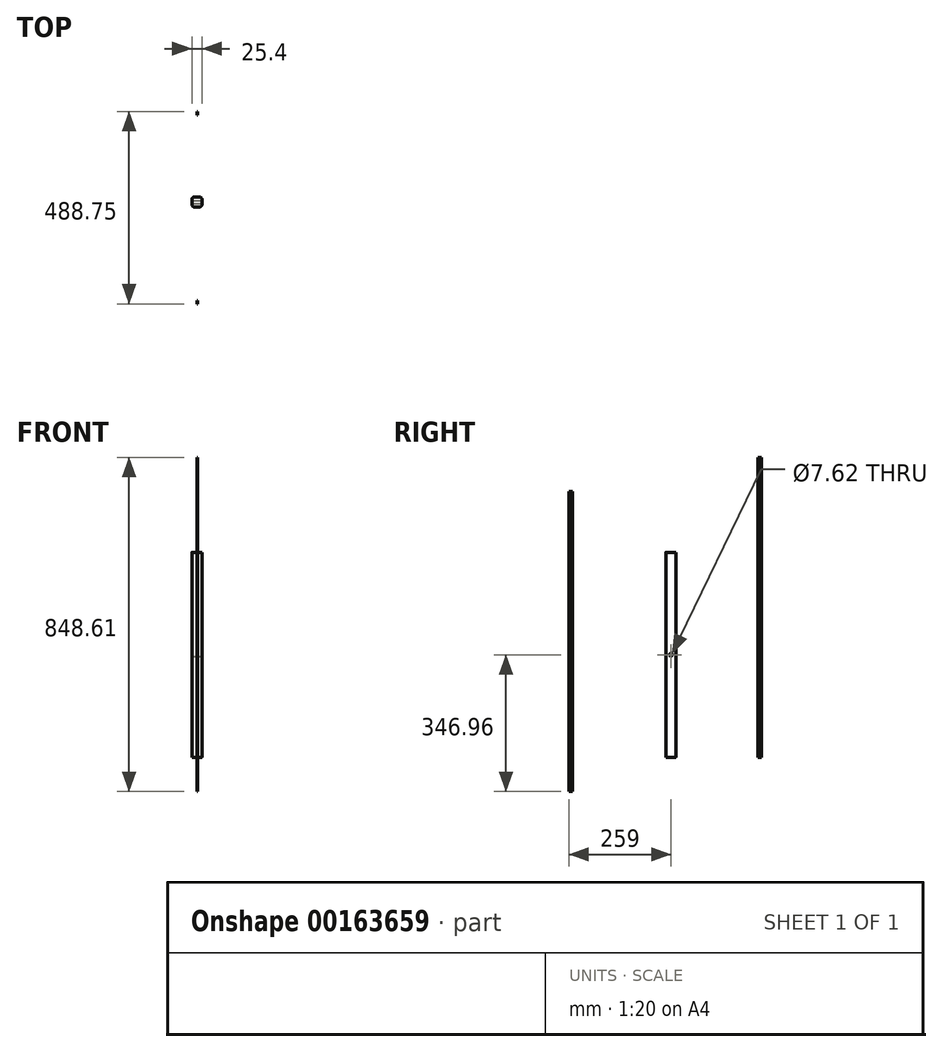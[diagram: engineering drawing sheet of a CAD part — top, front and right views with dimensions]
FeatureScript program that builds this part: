
annotation { "Feature Type Name" : "Feature", "Feature Type Description" : "" }
export const myFeature = defineFeature(function(context is Context, id is Id, definition is map)
    precondition{}
    {
        {
            var Q0;
            Q0=qCreatedBy(makeId("Top.planeOp"),FACE);
            var sketch = newSketch(context, id + "F0", { "sketchPlane" : qUnion([Q0])});
            skLineSegment(sketch, "E0.bottom", {"start": v(6.35, 12.7) * mm, "end": v(-6.35, 12.7) * mm});
            skLineSegment(sketch, "E0.top", {"start": v(6.35, -12.7) * mm, "end": v(-6.35, -12.7) * mm});
            skLineSegment(sketch, "E0.left", {"start": v(12.7, 6.35) * mm, "end": v(12.7, -6.35) * mm});
            skLineSegment(sketch, "E0.right", {"start": v(-12.7, 6.35) * mm, "end": v(-12.7, -6.35) * mm});
            skPoint(sketch, "E0.middle", {"position": v(0, 0) * mm});
            skPoint(sketch, "E1.visualSharp", {"position": v(-12.7, 12.7) * mm});
            skArc(sketch, "E1.filletArc", {"start": v(-6.35, 12.7) * mm, "mid": v(-10.84, 10.84) * mm, "end": v(-12.7, 6.35) * mm});
            skPoint(sketch, "E2.visualSharp", {"position": v(-12.7, -12.7) * mm});
            skArc(sketch, "E2.filletArc", {"start": v(-12.7, -6.35) * mm, "mid": v(-10.84, -10.84) * mm, "end": v(-6.35, -12.7) * mm});
            skPoint(sketch, "E3.visualSharp", {"position": v(12.7, -12.7) * mm});
            skArc(sketch, "E3.filletArc", {"start": v(6.35, -12.7) * mm, "mid": v(10.84, -10.84) * mm, "end": v(12.7, -6.35) * mm});
            skPoint(sketch, "E4.visualSharp", {"position": v(12.7, 12.7) * mm});
            skArc(sketch, "E4.filletArc", {"start": v(12.7, 6.35) * mm, "mid": v(10.84, 10.84) * mm, "end": v(6.35, 12.7) * mm});
            skSolve(sketch);
        }
        {
            var Q0;
            Q0=qSketchRegion(id+"F0",true);
            extrude(context, id + "F1", {"entities" : qUnion([Q0]), "depth" : 520.7 * mm});
        }
        {
            var Q0;
            Q0=qCreatedBy(makeId("Right.planeOp"),FACE);
            var sketch = newSketch(context, id + "F2", { "sketchPlane" : qUnion([Q0])});
            skLineSegment(sketch, "E5.bottom", {"start": v(-259, 675.39) * mm, "end": v(-250.53, 675.39) * mm});
            skLineSegment(sketch, "E5.top", {"start": v(-259, -86.61) * mm, "end": v(-250.53, -86.61) * mm});
            skLineSegment(sketch, "E5.left", {"start": v(-259, 675.39) * mm, "end": v(-259, -86.61) * mm});
            skLineSegment(sketch, "E5.right", {"start": v(-250.53, 675.39) * mm, "end": v(-250.53, -86.61) * mm});
            skSolve(sketch);
        }
        {
            var Q0;
            Q0=makeQuery(id+"F2.imprint","IMPRINT",FACE,{"disambiguationData":[TD([[makeQuery(id+"F2.imprint","IMPRINT",EDGE,{"derivedFrom":sQuery(id+"F2.wireOp",EDGE,"E5.bottom")}),-1.0]])]});
            extrude(context, id + "F3", {"entities" : qUnion([Q0]), "depth" : 1.27 * mm});
        }
        {
            var Q0;
            Q0=qCreatedBy(makeId("Right.planeOp"),FACE);
            var sketch = newSketch(context, id + "F4", { "sketchPlane" : qUnion([Q0])});
            skLineSegment(sketch, "E6.bottom", {"start": v(221.29, 762) * mm, "end": v(229.75, 762) * mm});
            skLineSegment(sketch, "E6.top", {"start": v(221.29, 0) * mm, "end": v(229.75, 0) * mm});
            skLineSegment(sketch, "E6.left", {"start": v(221.29, 762) * mm, "end": v(221.29, 0) * mm});
            skLineSegment(sketch, "E6.right", {"start": v(229.75, 762) * mm, "end": v(229.75, 0) * mm});
            skSolve(sketch);
        }
        {
            var Q0;
            Q0=makeQuery(id+"F4.imprint","IMPRINT",FACE,{"disambiguationData":[TD([[makeQuery(id+"F4.imprint","IMPRINT",EDGE,{"derivedFrom":sQuery(id+"F4.wireOp",EDGE,"E6.bottom")}),-1.0]])]});
            var Q1;
            Q1=sQuery(id+"F4.wireOp",EDGE,"E6.right");
            var Q2;
            Q2=sQuery(id+"F4.wireOp",EDGE,"E6.left");
            var Q3;
            Q3=sQuery(id+"F4.wireOp",EDGE,"E6.top");
            var Q4;
            Q4=sQuery(id+"F4.wireOp",EDGE,"E6.bottom");
            extrude(context, id + "F5", {"entities" : qUnion([Q0]), "surfaceEntities" : qUnion([Q1, Q2, Q3, Q4]), "depth" : 1.27 * mm});
        }
        {
            var Q0;
            Q0=makeQuery(id+"F1.opExtrude","SWEPT_FACE",FACE,{"disambiguationData":[OSD([sQuery(id+"F0.wireOp",EDGE,"E0.left")])]});
            var sketch = newSketch(context, id + "F6", { "sketchPlane" : qUnion([Q0])});
            skLineSegment(sketch, "E7", {"start": v(0, 520.7) * mm, "end": v(0, 260.35) * mm});
            skCircle(sketch, "E8", {"center": v(0, 260.35) * mm, "radius": 3.81 * mm});
            skSolve(sketch);
        }
        {
            var Q0;
            Q0=makeQuery(id+"F6.imprint","IMPRINT",FACE,{"disambiguationData":[TD([[makeQuery(id+"F6.imprint","IMPRINT",EDGE,{"derivedFrom":sQuery(id+"F6.wireOp",EDGE,"E8")}),1.0]])]});
            extrude(context, id + "F7", {"entities" : qUnion([Q0]), "operationType" : NewBodyOperationType.REMOVE, "oppositeDirection" : true, "depth" : 25.4 * mm});
        }
    });
